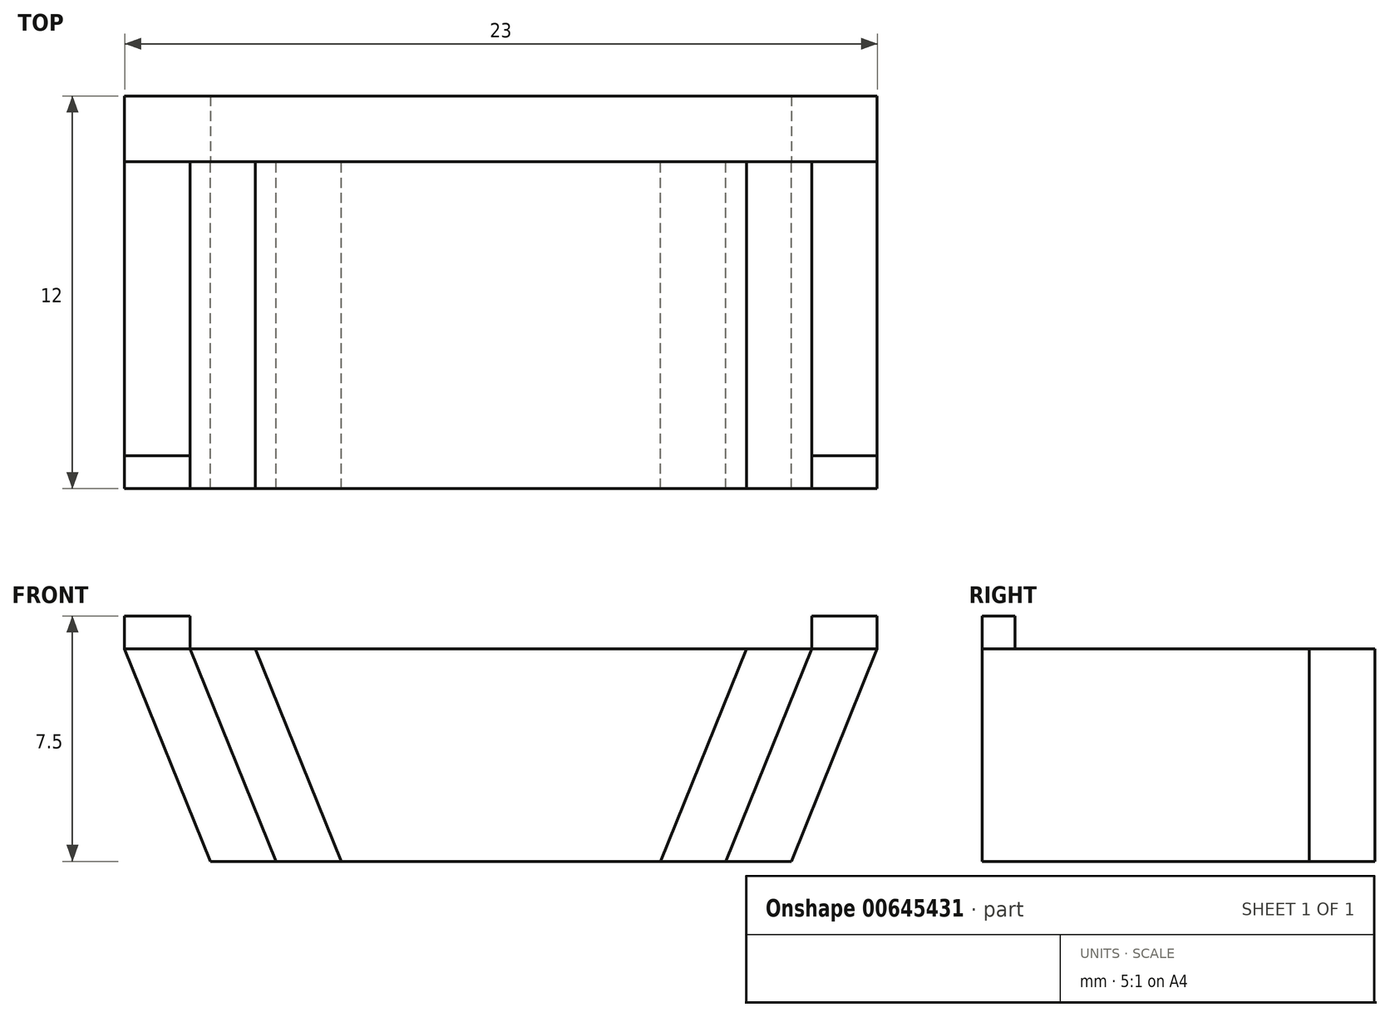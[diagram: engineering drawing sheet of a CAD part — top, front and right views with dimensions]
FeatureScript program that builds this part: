
annotation { "Feature Type Name" : "Feature", "Feature Type Description" : "" }
export const myFeature = defineFeature(function(context is Context, id is Id, definition is map)
    precondition{}
    {
        {
            var Q0;
            Q0=qCreatedBy(makeId("Front.planeOp"),FACE);
            var sketch = newSketch(context, id + "F0", { "sketchPlane" : qUnion([Q0])});
            skLineSegment(sketch, "E0", {"start": v(-2.63, 24.08) * mm, "end": v(12.37, 24.08) * mm});
            skLineSegment(sketch, "E1", {"start": v(-2.63, 24.08) * mm, "end": v(0, 17.58) * mm});
            skLineSegment(sketch, "E2", {"start": v(0, 17.58) * mm, "end": v(9.75, 17.58) * mm});
            skLineSegment(sketch, "E3", {"start": v(9.75, 17.58) * mm, "end": v(12.37, 24.08) * mm});
            skPoint(sketch, "E4", {"position": v(4.87, 24.08) * mm});
            skPoint(sketch, "E5", {"position": v(4.88, 17.58) * mm});
            skLineSegment(sketch, "E6", {"start": v(-2.63, 24.08) * mm, "end": v(-4.63, 24.08) * mm});
            skLineSegment(sketch, "E7", {"start": v(-4.63, 24.08) * mm, "end": v(-2, 17.58) * mm});
            skLineSegment(sketch, "E8", {"start": v(-2, 17.58) * mm, "end": v(0, 17.58) * mm});
            skLineSegment(sketch, "E9", {"start": v(12.37, 24.08) * mm, "end": v(14.37, 24.08) * mm});
            skLineSegment(sketch, "E10", {"start": v(14.37, 24.08) * mm, "end": v(11.75, 17.58) * mm});
            skLineSegment(sketch, "E11", {"start": v(11.75, 17.58) * mm, "end": v(9.75, 17.58) * mm});
            skLineSegment(sketch, "E12", {"start": v(-4.63, 24.08) * mm, "end": v(-6.63, 24.08) * mm});
            skLineSegment(sketch, "E13", {"start": v(-6.63, 24.08) * mm, "end": v(-4, 17.58) * mm});
            skLineSegment(sketch, "E14", {"start": v(-4, 17.58) * mm, "end": v(-2, 17.58) * mm});
            skLineSegment(sketch, "E15", {"start": v(14.37, 24.08) * mm, "end": v(16.37, 24.08) * mm});
            skLineSegment(sketch, "E16", {"start": v(16.37, 24.08) * mm, "end": v(13.75, 17.58) * mm});
            skLineSegment(sketch, "E17", {"start": v(13.75, 17.58) * mm, "end": v(11.75, 17.58) * mm});
            skSolve(sketch);
        }
        {
            var Q0;
            Q0=makeQuery(id+"F0.imprint","IMPRINT",FACE,{"disambiguationData":[TD([[makeQuery(id+"F0.imprint","IMPRINT",EDGE,{"derivedFrom":sQuery(id+"F0.wireOp",EDGE,"E0")}),-1.0]])]});
            var Q1;
            Q1=makeQuery(id+"F0.imprint","IMPRINT",FACE,{"disambiguationData":[TD([[makeQuery(id+"F0.imprint","IMPRINT",EDGE,{"derivedFrom":sQuery(id+"F0.wireOp",EDGE,"E7")}),-1.0]])]});
            var Q2;
            Q2=makeQuery(id+"F0.imprint","IMPRINT",FACE,{"disambiguationData":[TD([[makeQuery(id+"F0.imprint","IMPRINT",EDGE,{"derivedFrom":sQuery(id+"F0.wireOp",EDGE,"E10")}),1.0]])]});
            extrude(context, id + "F1", {"entities" : qUnion([Q0, Q1, Q2]), "depth" : 10 * mm, "offsetDistance" : 25 * mm});
        }
        {
            var Q0;
            Q0=makeQuery(id+"F0.imprint","IMPRINT",FACE,{"disambiguationData":[TD([[makeQuery(id+"F0.imprint","IMPRINT",EDGE,{"derivedFrom":sQuery(id+"F0.wireOp",EDGE,"E7")}),-1.0]])]});
            var Q1;
            Q1=makeQuery(id+"F0.imprint","IMPRINT",FACE,{"disambiguationData":[TD([[makeQuery(id+"F0.imprint","IMPRINT",EDGE,{"derivedFrom":sQuery(id+"F0.wireOp",EDGE,"E1")}),-1.0]])]});
            var Q2;
            Q2=makeQuery(id+"F0.imprint","IMPRINT",FACE,{"disambiguationData":[TD([[makeQuery(id+"F0.imprint","IMPRINT",EDGE,{"derivedFrom":sQuery(id+"F0.wireOp",EDGE,"E0")}),-1.0]])]});
            var Q3;
            Q3=makeQuery(id+"F0.imprint","IMPRINT",FACE,{"disambiguationData":[TD([[makeQuery(id+"F0.imprint","IMPRINT",EDGE,{"derivedFrom":sQuery(id+"F0.wireOp",EDGE,"E3")}),-1.0]])]});
            var Q4;
            Q4=makeQuery(id+"F0.imprint","IMPRINT",FACE,{"disambiguationData":[TD([[makeQuery(id+"F0.imprint","IMPRINT",EDGE,{"derivedFrom":sQuery(id+"F0.wireOp",EDGE,"E10")}),1.0]])]});
            extrude(context, id + "F2", {"entities" : qUnion([Q0, Q1, Q2, Q3, Q4]), "depth" : -2 * mm, "offsetDistance" : 25 * mm});
        }
        {
            var Q0;
            Q0=makeQuery(id+"F1.opExtrude","SWEPT_FACE",FACE,{"disambiguationData":[OSD([sQuery(id+"F0.wireOp",EDGE,"E12")])]});
            var sketch = newSketch(context, id + "F3", { "sketchPlane" : qUnion([Q0])});
            skLineSegment(sketch, "E18.0.0", {"start": v(-4.63, 0) * mm, "end": v(-6.63, 0) * mm});
            skLineSegment(sketch, "E18.0.1", {"start": v(-6.63, 0) * mm, "end": v(-6.63, -10) * mm});
            skLineSegment(sketch, "E18.0.2", {"start": v(-6.63, -10) * mm, "end": v(-4.63, -10) * mm});
            skLineSegment(sketch, "E18.0.3", {"start": v(-4.63, -10) * mm, "end": v(-4.63, 0) * mm});
            skLineSegment(sketch, "E19.0.0", {"start": v(16.37, 0) * mm, "end": v(14.37, 0) * mm});
            skLineSegment(sketch, "E19.0.1", {"start": v(14.37, 0) * mm, "end": v(14.37, -10) * mm});
            skLineSegment(sketch, "E19.0.2", {"start": v(14.37, -10) * mm, "end": v(16.37, -10) * mm});
            skLineSegment(sketch, "E19.0.3", {"start": v(16.37, -10) * mm, "end": v(16.37, 0) * mm});
            skLineSegment(sketch, "E20.top", {"start": v(-6.63, -9) * mm, "end": v(-4.63, -9) * mm});
            skLineSegment(sketch, "E20.left", {"start": v(-6.63, -10) * mm, "end": v(-6.63, -9) * mm});
            skLineSegment(sketch, "E20.right", {"start": v(-4.63, -10) * mm, "end": v(-4.63, -9) * mm});
            skLineSegment(sketch, "E21.left", {"start": v(14.37, -10) * mm, "end": v(14.37, -9) * mm});
            skLineSegment(sketch, "E21.right", {"start": v(16.37, -10) * mm, "end": v(16.37, -9) * mm});
            skLineSegment(sketch, "E22", {"start": v(14.37, -9) * mm, "end": v(16.37, -9) * mm});
            skSolve(sketch);
        }
        {
            var Q0;
            Q0=makeQuery(id+"F3.imprint","IMPRINT",FACE,{"disambiguationData":[TD([[makeQuery(id+"F3.imprint","IMPRINT",EDGE,{"derivedFrom":sQuery(id+"F3.wireOp",EDGE,"E18.0.2")}),-1.0]])]});
            var Q1;
            Q1=makeQuery(id+"F3.imprint","IMPRINT",FACE,{"disambiguationData":[TD([[makeQuery(id+"F3.imprint","IMPRINT",EDGE,{"derivedFrom":sQuery(id+"F3.wireOp",EDGE,"E19.0.2")}),1.0]])]});
            extrude(context, id + "F4", {"entities" : qUnion([Q0, Q1]), "depth" : 1 * mm, "offsetDistance" : 25 * mm});
        }
    });
